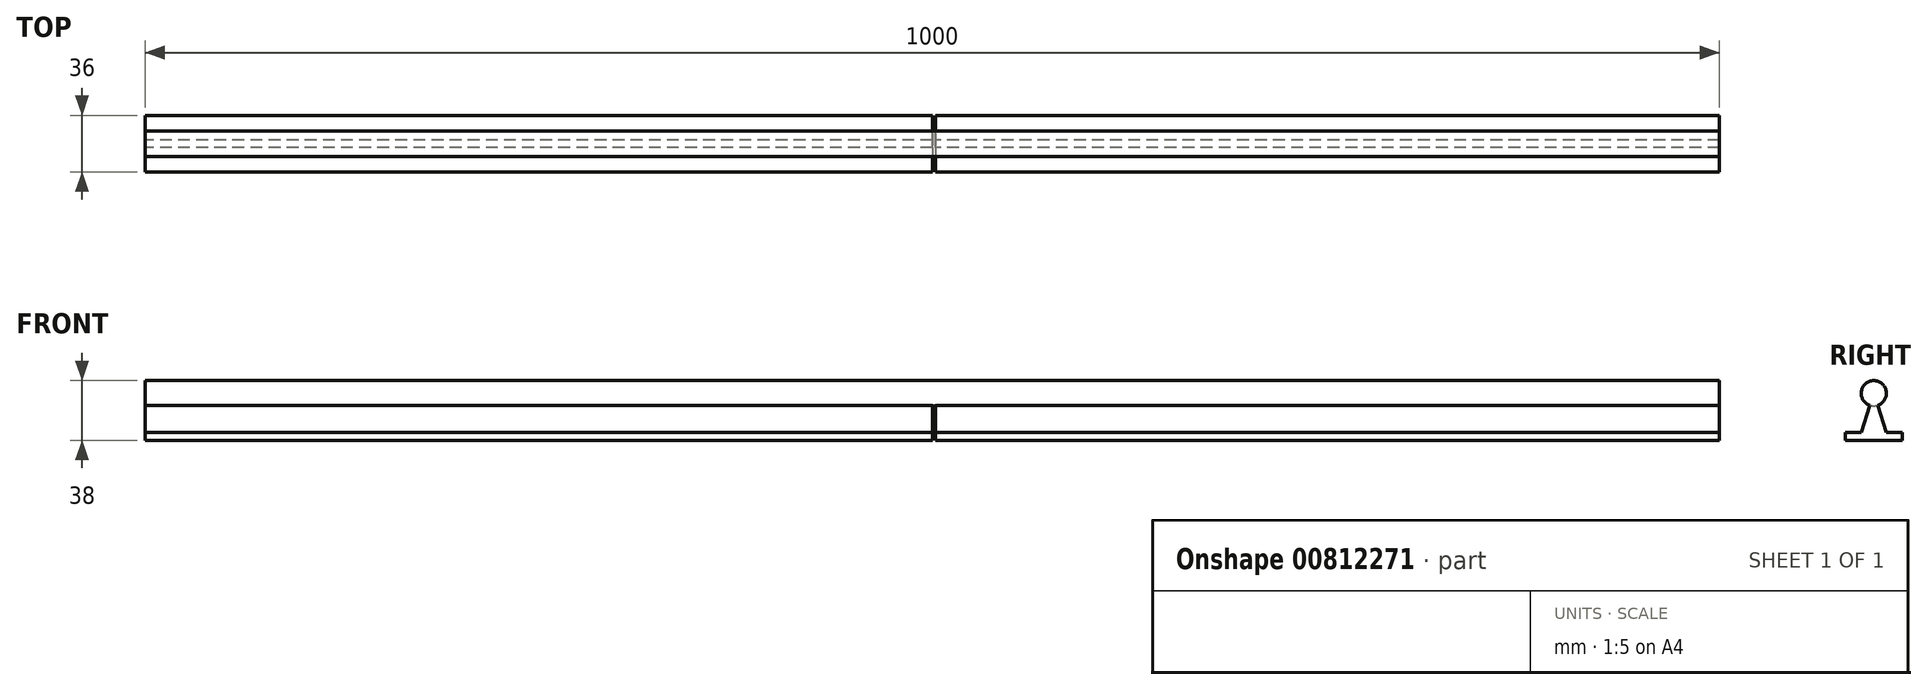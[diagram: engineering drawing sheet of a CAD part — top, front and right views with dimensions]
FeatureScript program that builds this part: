
annotation { "Feature Type Name" : "Feature", "Feature Type Description" : "" }
export const myFeature = defineFeature(function(context is Context, id is Id, definition is map)
    precondition{}
    {
        {
            var Q0;
            Q0=qCreatedBy(makeId("Right.planeOp"),FACE);
            var sketch = newSketch(context, id + "F0", { "sketchPlane" : qUnion([Q0])});
            skCircle(sketch, "E0", {"center": v(0, 0) * mm, "radius": 8 * mm});
            skLineSegment(sketch, "E1", {"start": v(0, 0) * mm, "end": v(8, -25) * mm});
            skLineSegment(sketch, "E2", {"start": v(8, -25) * mm, "end": v(0, -25) * mm});
            skLineSegment(sketch, "E3", {"start": v(0, 0) * mm, "end": v(0, -25) * mm, "construction": true});
            skLineSegment(sketch, "E4.MirrorCS", {"start": v(0, 0) * mm, "end": v(-8, -25) * mm});
            skLineSegment(sketch, "E5.MirrorCS", {"start": v(-8, -25) * mm, "end": v(0, -25) * mm});
            skLineSegment(sketch, "E6.bottom", {"start": v(18, -25) * mm, "end": v(-18, -25) * mm});
            skLineSegment(sketch, "E6.top", {"start": v(18, -30) * mm, "end": v(-18, -30) * mm});
            skLineSegment(sketch, "E6.left", {"start": v(18, -25) * mm, "end": v(18, -30) * mm});
            skLineSegment(sketch, "E6.right", {"start": v(-18, -25) * mm, "end": v(-18, -30) * mm});
            skPoint(sketch, "E6.middle", {"position": v(0, -27.5) * mm});
            skSolve(sketch);
        }
        {
            var Q0;
            {var subQ0=sQuery(id+"F0.wireOp",EDGE,"E1");var subQ1=sQuery(id+"F0.wireOp",EDGE,"E0");var subQ2=makeQuery(id+"F0.imprint","INTERSECT",VERTEX,{"derivedFrom":[subQ1,subQ0]});Q0=makeQuery(id+"F0.imprint","IMPRINT",FACE,{"disambiguationData":[TD([[makeQuery(id+"F0.imprint","IMPRINT",EDGE,{"disambiguationData":[TD([[subQ2,-1.0]])],"derivedFrom":subQ1}),1.0]])]});}
            var Q1;
            {var subQ0=sQuery(id+"F0.wireOp",EDGE,"E1");var subQ1=sQuery(id+"F0.wireOp",EDGE,"E0");var subQ2=makeQuery(id+"F0.imprint","INTERSECT",VERTEX,{"derivedFrom":[subQ1,subQ0]});Q1=makeQuery(id+"F0.imprint","IMPRINT",FACE,{"disambiguationData":[TD([[makeQuery(id+"F0.imprint","IMPRINT",EDGE,{"disambiguationData":[TD([[subQ2,1.0]])],"derivedFrom":subQ1}),1.0]])]});}
            var Q2;
            {var subQ0=sQuery(id+"F0.wireOp",EDGE,"E1");var subQ1=sQuery(id+"F0.wireOp",EDGE,"E0");var subQ2=makeQuery(id+"F0.imprint","INTERSECT",VERTEX,{"derivedFrom":[subQ1,subQ0]});Q2=makeQuery(id+"F0.imprint","IMPRINT",FACE,{"disambiguationData":[TD([[makeQuery(id+"F0.imprint","IMPRINT",EDGE,{"disambiguationData":[TD([[subQ2,1.0]])],"derivedFrom":subQ1}),-1.0]])]});}
            var Q3;
            Q3=makeQuery(id+"F0.imprint","IMPRINT",FACE,{"disambiguationData":[TD([[makeQuery(id+"F0.imprint","IMPRINT",EDGE,{"derivedFrom":sQuery(id+"F0.wireOp",EDGE,"E6.top")}),-1.0]])]});
            extrude(context, id + "F1", {"entities" : qUnion([Q0, Q1, Q2, Q3]), "endBound" : BoundingType.SYMMETRIC, "depth" : 1000 * mm, "offsetDistance" : 25 * mm});
        }
        {
            var Q0;
            {var subQ0=sQuery(id+"F0.wireOp",EDGE,"E1");var subQ1=sQuery(id+"F0.wireOp",EDGE,"E0");var subQ2=makeQuery(id+"F0.imprint","INTERSECT",VERTEX,{"derivedFrom":[subQ1,subQ0]});Q0=makeQuery(id+"F0.imprint","IMPRINT",FACE,{"disambiguationData":[TD([[makeQuery(id+"F0.imprint","IMPRINT",EDGE,{"disambiguationData":[TD([[subQ2,1.0]])],"derivedFrom":subQ1}),-1.0]])]});}
            var Q1;
            Q1=makeQuery(id+"F0.imprint","IMPRINT",FACE,{"disambiguationData":[TD([[makeQuery(id+"F0.imprint","IMPRINT",EDGE,{"derivedFrom":sQuery(id+"F0.wireOp",EDGE,"E6.top")}),-1.0]])]});
            extrude(context, id + "F2", {"entities" : qUnion([Q0, Q1]), "operationType" : NewBodyOperationType.REMOVE, "depth" : 2 * mm, "offsetDistance" : 25 * mm});
        }
    });
